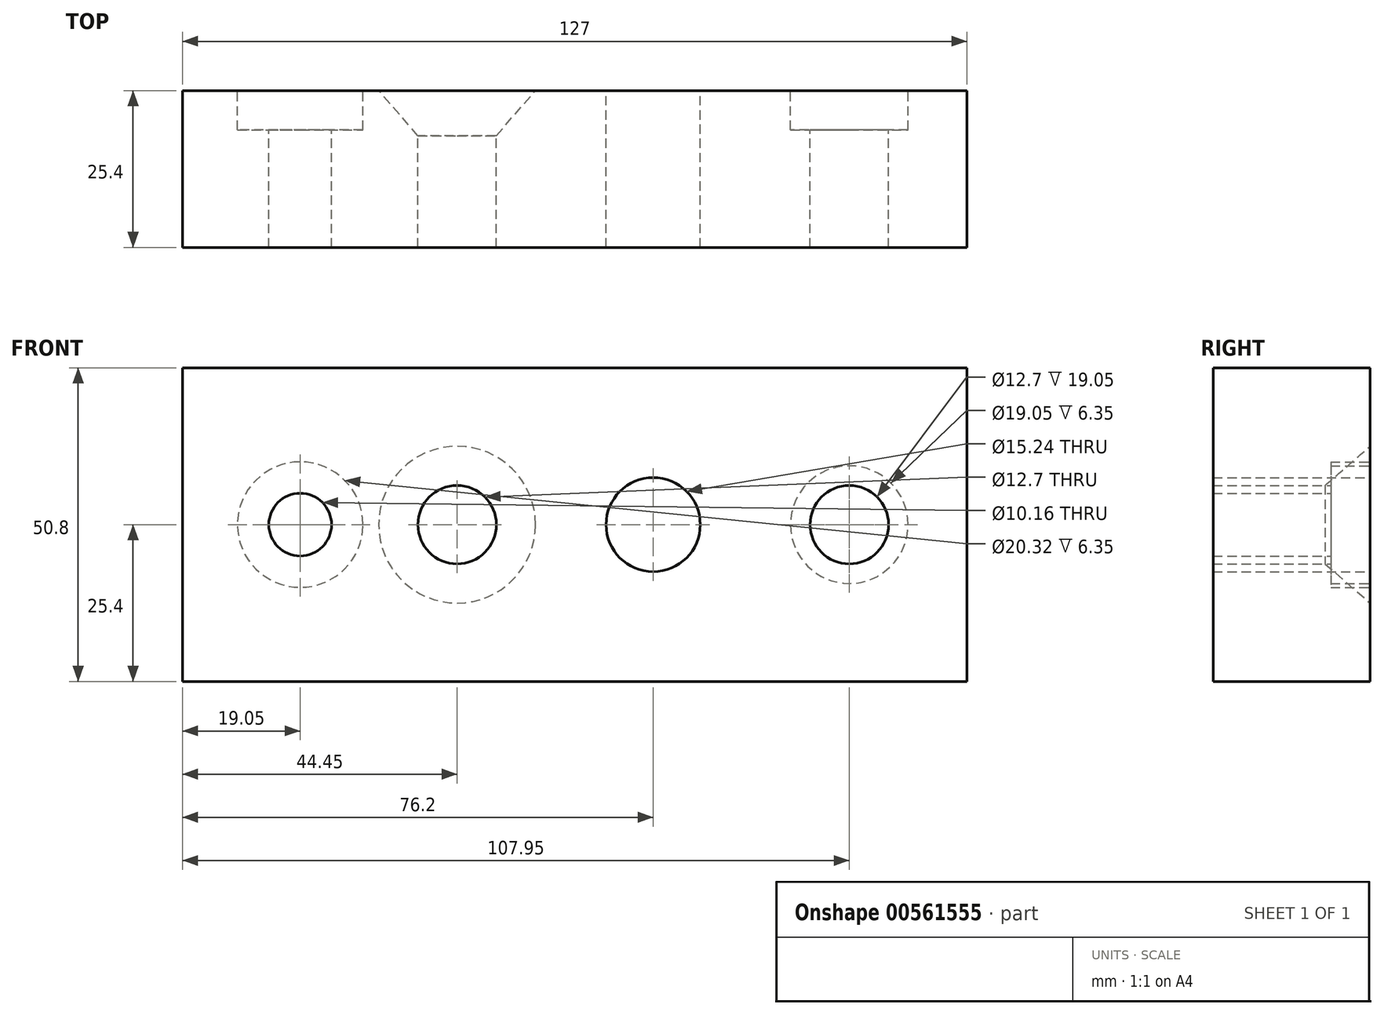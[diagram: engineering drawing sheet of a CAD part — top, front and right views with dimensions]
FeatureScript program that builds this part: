
annotation { "Feature Type Name" : "Feature", "Feature Type Description" : "" }
export const myFeature = defineFeature(function(context is Context, id is Id, definition is map)
    precondition{}
    {
        {
            var Q0;
            Q0=qCreatedBy(makeId("Front.planeOp"),FACE);
            var sketch = newSketch(context, id + "F0", { "sketchPlane" : qUnion([Q0])});
            skLineSegment(sketch, "E0", {"start": v(0, 0) * mm, "end": v(127, 0) * mm});
            skLineSegment(sketch, "E1", {"start": v(127, 0) * mm, "end": v(127, 50.8) * mm});
            skLineSegment(sketch, "E2", {"start": v(127, 50.8) * mm, "end": v(0, 50.8) * mm});
            skLineSegment(sketch, "E3", {"start": v(0, 50.8) * mm, "end": v(0, 0) * mm});
            skLineSegment(sketch, "E4", {"start": v(0, 25.4) * mm, "end": v(19.05, 25.4) * mm});
            skLineSegment(sketch, "E5", {"start": v(19.05, 25.4) * mm, "end": v(44.45, 25.4) * mm});
            skLineSegment(sketch, "E6", {"start": v(44.45, 25.4) * mm, "end": v(76.2, 25.4) * mm});
            skLineSegment(sketch, "E7", {"start": v(76.2, 25.4) * mm, "end": v(107.95, 25.4) * mm});
            skPoint(sketch, "E8", {"position": v(19.05, 25.4) * mm});
            skPoint(sketch, "E9", {"position": v(44.45, 25.4) * mm});
            skPoint(sketch, "E10", {"position": v(76.2, 25.4) * mm});
            skPoint(sketch, "E11", {"position": v(107.95, 25.4) * mm});
            skPoint(sketch, "E12", {"position": v(-55.14, 77.74) * mm});
            skSolve(sketch);
        }
        {
            var Q0;
            {var subQ3=sQuery(id+"F0.wireOp",EDGE,"E0");Q0=makeQuery(id+"F0.imprint","IMPRINT",FACE,{"disambiguationData":[TD([[makeQuery(id+"F0.imprint","IMPRINT",EDGE,{"derivedFrom":subQ3}),1.0]])]});}
            extrude(context, id + "F1", {"entities" : qUnion([Q0]), "depth" : 25.4 * mm, "offsetDistance" : 25.4 * mm});
        }
        {
            var Q0;
            Q0=sQuery(id+"F0.wireOp",VERTEX,"E11");
            var Q1;
            Q1=makeQuery(id+"F1.opExtrude","SWEPT_BODY",BODY,{"disambiguationData":[OSD([sQuery(id+"F0.wireOp",EDGE,"E0"),sQuery(id+"F0.wireOp",EDGE,"E1"),sQuery(id+"F0.wireOp",EDGE,"E2"),sQuery(id+"F0.wireOp",EDGE,"E3")])]});
            hole(context, id + "F2", {"style" : HoleStyle.C_BORE, "endStyle" : HoleEndStyle.THROUGH, "oppositeDirection" : true, "holeDiameter" : 12.7 * mm, "cBoreDiameter" : 19.05 * mm, "cBoreDepth" : 6.35 * mm, "isTappedThrough" : true, "tappedDepth" : 12.7 * mm, "tapClearance" : 3, "locations" : qUnion([Q0]), "scope" : qUnion([Q1])});
        }
        {
            var Q0;
            Q0=sQuery(id+"F0.wireOp",VERTEX,"E10");
            var Q1;
            Q1=makeQuery(id+"F1.opExtrude","SWEPT_BODY",BODY,{"disambiguationData":[OSD([sQuery(id+"F0.wireOp",EDGE,"E0"),sQuery(id+"F0.wireOp",EDGE,"E1"),sQuery(id+"F0.wireOp",EDGE,"E2"),sQuery(id+"F0.wireOp",EDGE,"E3")])]});
            hole(context, id + "F3", {"style" : HoleStyle.SIMPLE, "endStyle" : HoleEndStyle.THROUGH, "oppositeDirection" : true, "holeDiameter" : 15.24 * mm, "isTappedThrough" : true, "tappedDepth" : 12.7 * mm, "tapClearance" : 3, "locations" : qUnion([Q0]), "scope" : qUnion([Q1])});
        }
        {
            var Q0;
            Q0=sQuery(id+"F0.wireOp",VERTEX,"E9");
            var Q1;
            Q1=makeQuery(id+"F1.opExtrude","SWEPT_BODY",BODY,{"disambiguationData":[OSD([sQuery(id+"F0.wireOp",EDGE,"E0"),sQuery(id+"F0.wireOp",EDGE,"E1"),sQuery(id+"F0.wireOp",EDGE,"E2"),sQuery(id+"F0.wireOp",EDGE,"E3")])]});
            hole(context, id + "F4", {"style" : HoleStyle.C_SINK, "endStyle" : HoleEndStyle.THROUGH, "oppositeDirection" : true, "holeDiameter" : 12.7 * mm, "cSinkDiameter" : 25.4 * mm, "cSinkAngle" : 82 * degree, "isTappedThrough" : true, "tappedDepth" : 12.7 * mm, "tapClearance" : 3, "locations" : qUnion([Q0]), "scope" : qUnion([Q1])});
        }
        {
            var Q0;
            Q0=sQuery(id+"F0.wireOp",VERTEX,"E8");
            var Q1;
            Q1=makeQuery(id+"F1.opExtrude","SWEPT_BODY",BODY,{"disambiguationData":[OSD([sQuery(id+"F0.wireOp",EDGE,"E0"),sQuery(id+"F0.wireOp",EDGE,"E1"),sQuery(id+"F0.wireOp",EDGE,"E2"),sQuery(id+"F0.wireOp",EDGE,"E3")])]});
            hole(context, id + "F5", {"style" : HoleStyle.C_BORE, "endStyle" : HoleEndStyle.THROUGH, "oppositeDirection" : true, "holeDiameter" : 10.16 * mm, "cBoreDiameter" : 20.32 * mm, "cBoreDepth" : 6.35 * mm, "isTappedThrough" : true, "tappedDepth" : 12.7 * mm, "tapClearance" : 3, "locations" : qUnion([Q0]), "scope" : qUnion([Q1])});
        }
    });
